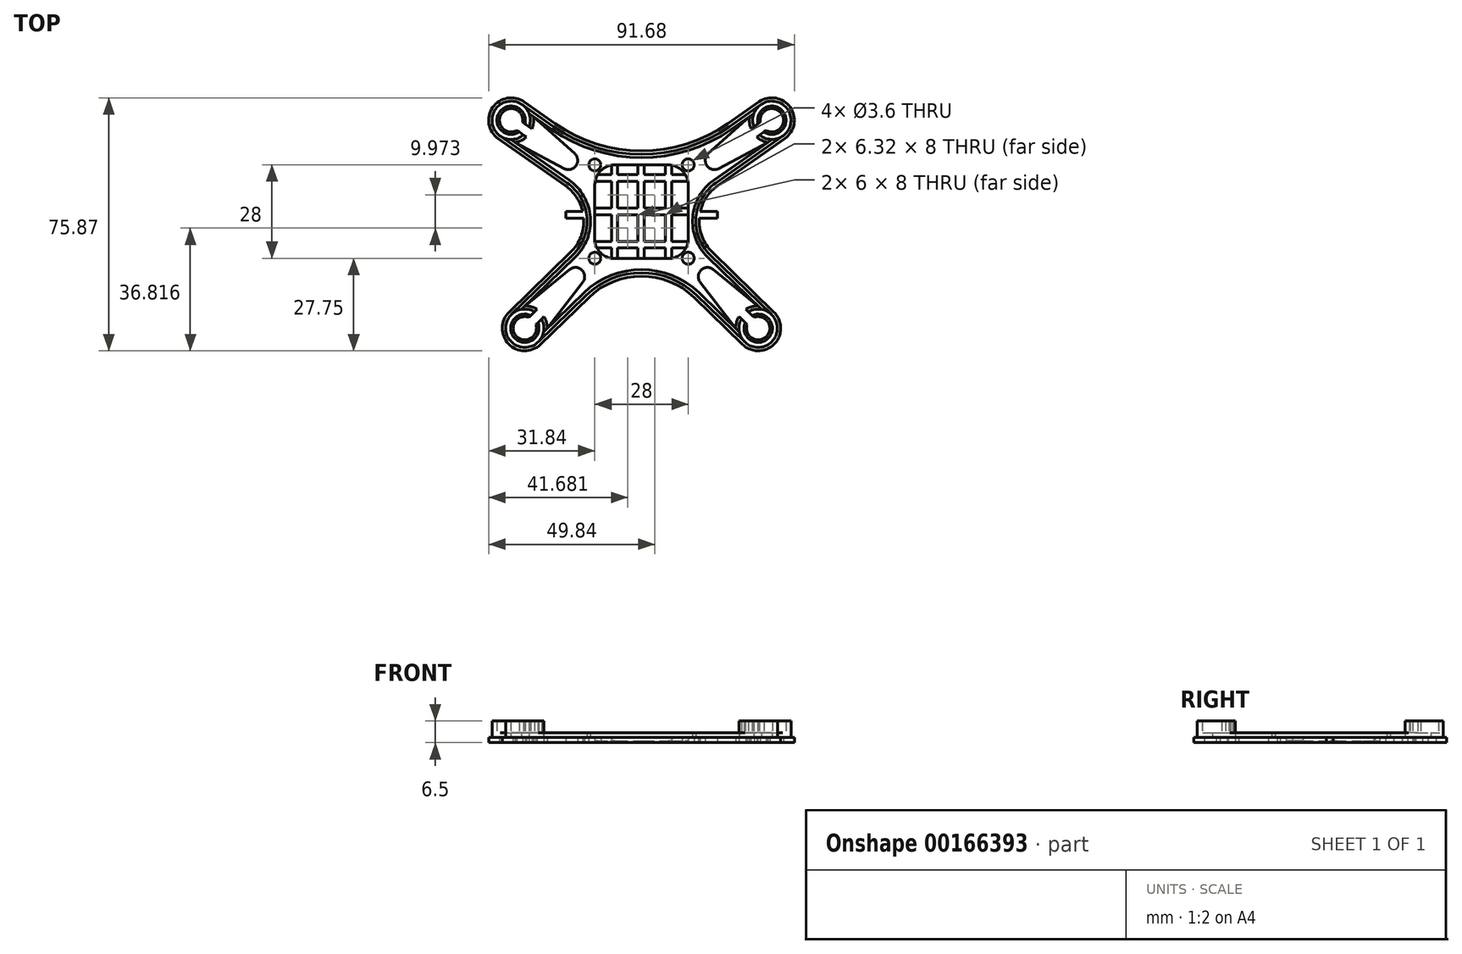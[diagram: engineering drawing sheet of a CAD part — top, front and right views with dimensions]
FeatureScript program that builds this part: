
annotation { "Feature Type Name" : "Feature", "Feature Type Description" : "" }
export const myFeature = defineFeature(function(context is Context, id is Id, definition is map)
    precondition{}
    {
        {
            var Q0;
            Q0=qCreatedBy(makeId("Top.planeOp"),FACE);
            var sketch = newSketch(context, id + "F0", { "sketchPlane" : qUnion([Q0])});
            skArc(sketch, "E0", {"start": v(31.69, -33.87) * mm, "mid": v(37.5, -37.44) * mm, "end": v(33.78, -31.72) * mm});
            skArc(sketch, "E1", {"start": v(29.24, -31.49) * mm, "mid": v(28.5, -33.2) * mm, "end": v(28.25, -35.06) * mm});
            skCircle(sketch, "E2", {"center": v(14, -14) * mm, "radius": 1.8 * mm});
            skLineSegment(sketch, "E3.0", {"start": v(39.7, -30.16) * mm, "end": v(21.24, -12.21) * mm});
            skLineSegment(sketch, "E4.0", {"start": v(30.3, -39.84) * mm, "end": v(15.88, -25.83) * mm});
            skArc(sketch, "E5.MirrorCS", {"start": v(-15.88, -25.83) * mm, "mid": v(0, -19.38) * mm, "end": v(15.88, -25.83) * mm});
            skPoint(sketch, "E6.orphan", {"position": v(7.32, -17.5) * mm});
            skArc(sketch, "E7", {"start": v(21.52, -17.39) * mm, "mid": v(17.87, -17.55) * mm, "end": v(17.6, -21.2) * mm});
            skLineSegment(sketch, "E8", {"start": v(31.69, -33.87) * mm, "end": v(29.24, -31.49) * mm});
            skLineSegment(sketch, "E9", {"start": v(31.33, -29.34) * mm, "end": v(33.78, -31.72) * mm});
            skArc(sketch, "E10.trimOffspring", {"start": v(34.87, -28.25) * mm, "mid": v(33.02, -28.55) * mm, "end": v(31.33, -29.34) * mm});
            skArc(sketch, "E11.trimOffspring", {"start": v(30.3, -39.84) * mm, "mid": v(39.84, -39.7) * mm, "end": v(39.7, -30.16) * mm});
            skArc(sketch, "E12.filletArc", {"start": v(9, -14) * mm, "mid": v(12.31, -12.31) * mm, "end": v(14, -9) * mm});
            skLineSegment(sketch, "E13", {"start": v(28.25, -35.06) * mm, "end": v(17.6, -21.2) * mm});
            skLineSegment(sketch, "E14", {"start": v(34.87, -28.25) * mm, "end": v(21.52, -17.39) * mm});
            skArc(sketch, "E15", {"start": v(37.36, 24.33) * mm, "mid": v(41.96, 29.38) * mm, "end": v(35.64, 26.79) * mm});
            skArc(sketch, "E16", {"start": v(34.56, 22.37) * mm, "mid": v(36.1, 21.32) * mm, "end": v(37.89, 20.73) * mm});
            skLineSegment(sketch, "E17", {"start": v(14, -9) * mm, "end": v(14, 8) * mm});
            skCircle(sketch, "E18", {"center": v(14, 14) * mm, "radius": 1.8 * mm});
            skLineSegment(sketch, "E19", {"start": v(8, 14) * mm, "end": v(0, 14) * mm});
            skArc(sketch, "E20.filletArc", {"start": v(14, 8) * mm, "mid": v(12.24, 12.24) * mm, "end": v(8, 14) * mm});
            skArc(sketch, "E21", {"start": v(20.05, 17.37) * mm, "mid": v(19.64, 13.75) * mm, "end": v(23.18, 12.9) * mm});
            skLineSegment(sketch, "E22.0", {"start": v(22.85, 7.76) * mm, "end": v(42.96, 21.84) * mm});
            skLineSegment(sketch, "E23.0", {"start": v(25.81, 26.31) * mm, "end": v(35.22, 32.9) * mm});
            skLineSegment(sketch, "E24", {"start": v(37.89, 20.73) * mm, "end": v(23.18, 12.9) * mm});
            skLineSegment(sketch, "E25", {"start": v(32.44, 28.51) * mm, "end": v(20.05, 17.37) * mm});
            skLineSegment(sketch, "E26.trimOffspring", {"start": v(34.56, 22.37) * mm, "end": v(37.36, 24.33) * mm});
            skLineSegment(sketch, "E27.trimOffspring", {"start": v(32.84, 24.83) * mm, "end": v(35.64, 26.79) * mm});
            skArc(sketch, "E28.trimOffspring", {"start": v(32.44, 28.51) * mm, "mid": v(32.38, 26.64) * mm, "end": v(32.84, 24.83) * mm});
            skArc(sketch, "E29.trimOffspring", {"start": v(42.96, 21.84) * mm, "mid": v(44.62, 31.24) * mm, "end": v(35.22, 32.9) * mm});
            skArc(sketch, "E30.filletArc", {"start": v(22.85, 7.76) * mm, "mid": v(17.35, -1.85) * mm, "end": v(21.24, -12.21) * mm});
            skArc(sketch, "E31.MirrorCS", {"start": v(-32.44, 28.51) * mm, "mid": v(-32.38, 26.64) * mm, "end": v(-32.84, 24.83) * mm});
            skLineSegment(sketch, "E32.MirrorCS", {"start": v(-32.84, 24.83) * mm, "end": v(-35.64, 26.79) * mm});
            skLineSegment(sketch, "E33.MirrorCS", {"start": v(-34.56, 22.37) * mm, "end": v(-37.36, 24.33) * mm});
            skLineSegment(sketch, "E34.MirrorCS", {"start": v(-31.69, -33.87) * mm, "end": v(-29.24, -31.49) * mm});
            skArc(sketch, "E35.MirrorCS", {"start": v(-34.87, -28.25) * mm, "mid": v(-33.02, -28.55) * mm, "end": v(-31.33, -29.34) * mm});
            skArc(sketch, "E36.MirrorCS", {"start": v(-29.24, -31.49) * mm, "mid": v(-28.5, -33.2) * mm, "end": v(-28.25, -35.06) * mm});
            skArc(sketch, "E37.MirrorCS", {"start": v(-34.56, 22.37) * mm, "mid": v(-36.1, 21.32) * mm, "end": v(-37.89, 20.73) * mm});
            skLineSegment(sketch, "E38.MirrorCS", {"start": v(-31.33, -29.34) * mm, "end": v(-33.78, -31.72) * mm});
            skCircle(sketch, "E39.MirrorC", {"center": v(-14, -14) * mm, "radius": 1.8 * mm});
            skArc(sketch, "E40.MirrorCS", {"start": v(-9, -14) * mm, "mid": v(-12.31, -12.31) * mm, "end": v(-14, -9) * mm});
            skLineSegment(sketch, "E41.MirrorCS", {"start": v(-25.81, 26.31) * mm, "end": v(-35.22, 32.9) * mm});
            skArc(sketch, "E42.MirrorCS", {"start": v(-31.69, -33.87) * mm, "mid": v(-37.5, -37.44) * mm, "end": v(-33.78, -31.72) * mm});
            skLineSegment(sketch, "E43.MirrorCS", {"start": v(-22.85, 7.76) * mm, "end": v(-42.96, 21.84) * mm});
            skLineSegment(sketch, "E44.MirrorCS", {"start": v(-37.89, 20.73) * mm, "end": v(-23.18, 12.9) * mm});
            skPoint(sketch, "E45.MirrorP", {"position": v(-7.32, -17.5) * mm});
            skLineSegment(sketch, "E46.MirrorCS", {"start": v(-14, -9) * mm, "end": v(-14, 8) * mm});
            skCircle(sketch, "E47.MirrorC", {"center": v(-14, 14) * mm, "radius": 1.8 * mm});
            skLineSegment(sketch, "E48.MirrorCS", {"start": v(-32.44, 28.51) * mm, "end": v(-20.05, 17.37) * mm});
            skArc(sketch, "E49.MirrorCS", {"start": v(-21.52, -17.39) * mm, "mid": v(-17.87, -17.55) * mm, "end": v(-17.6, -21.2) * mm});
            skArc(sketch, "E50.MirrorCS", {"start": v(-14, 8) * mm, "mid": v(-12.24, 12.24) * mm, "end": v(-8, 14) * mm});
            skLineSegment(sketch, "E51.MirrorCS", {"start": v(-8, 14) * mm, "end": v(0, 14) * mm});
            skArc(sketch, "E52.MirrorCS", {"start": v(-37.36, 24.33) * mm, "mid": v(-41.96, 29.38) * mm, "end": v(-35.64, 26.79) * mm});
            skArc(sketch, "E53.MirrorCS", {"start": v(-22.85, 7.76) * mm, "mid": v(-17.35, -1.85) * mm, "end": v(-21.24, -12.21) * mm});
            skArc(sketch, "E54.MirrorCS", {"start": v(-20.05, 17.37) * mm, "mid": v(-19.64, 13.75) * mm, "end": v(-23.18, 12.9) * mm});
            skLineSegment(sketch, "E55.MirrorCS", {"start": v(-28.25, -35.06) * mm, "end": v(-17.6, -21.2) * mm});
            skArc(sketch, "E56.MirrorCS", {"start": v(-42.96, 21.84) * mm, "mid": v(-44.62, 31.24) * mm, "end": v(-35.22, 32.9) * mm});
            skLineSegment(sketch, "E57.MirrorCS", {"start": v(-30.3, -39.84) * mm, "end": v(-15.88, -25.83) * mm});
            skLineSegment(sketch, "E58.MirrorCS", {"start": v(-39.7, -30.16) * mm, "end": v(-21.24, -12.21) * mm});
            skLineSegment(sketch, "E59.MirrorCS", {"start": v(-34.87, -28.25) * mm, "end": v(-21.52, -17.39) * mm});
            skArc(sketch, "E60.MirrorCS", {"start": v(-30.3, -39.84) * mm, "mid": v(-39.84, -39.7) * mm, "end": v(-39.7, -30.16) * mm});
            skPoint(sketch, "E61.orphan", {"position": v(-8.23, 14) * mm});
            skPoint(sketch, "E62.orphan", {"position": v(8.23, 14) * mm});
            skArc(sketch, "E63.filletArc", {"start": v(-25.81, 26.31) * mm, "mid": v(0, 18.18) * mm, "end": v(25.81, 26.31) * mm});
            skLineSegment(sketch, "E64.trimOffspring", {"start": v(9, -14) * mm, "end": v(0, -14) * mm});
            skLineSegment(sketch, "E65.trimOffspring", {"start": v(-9, -14) * mm, "end": v(0, -14) * mm});
            skSolve(sketch);
        }
        {
            var Q0;
            Q0=qSketchRegion(id+"F0",true);
            extrude(context, id + "F1", {"entities" : qUnion([Q0]), "depth" : 1.5 * mm});
        }
        {
            var Q0;
            Q0=makeQuery(id+"F1.opExtrude","CAP_FACE",FACE,{"disambiguationData":[OSD([sQuery(id+"F0.wireOp",EDGE,"E0"),sQuery(id+"F0.wireOp",EDGE,"E1"),sQuery(id+"F0.wireOp",EDGE,"a01uJ8fQ-2ShT-JJJs-khPB-feFI2KhJfNbK"),sQuery(id+"F0.wireOp",EDGE,"Ob7BAK0L-Im8b-nV2W-ZPOP-jmZc5u1GQHVQ"),sQuery(id+"F0.wireOp",EDGE,"Yhxhbh3N-Pwvf-CZAK-NTRz-WfjfcWOoB3H8"),sQuery(id+"F0.wireOp",EDGE,"E2"),sQuery(id+"F0.wireOp",EDGE,"E3.0"),sQuery(id+"F0.wireOp",EDGE,"E4.0"),sQuery(id+"F0.wireOp",EDGE,"921c4a34-4074-4e6a-8ea0-2c27b11e1a93.0"),sQuery(id+"F0.wireOp",EDGE,"8042876e-c550-468f-ba5b-50dd2e758e40.0"),sQuery(id+"F0.wireOp",EDGE,"gIcWUmLJ-M7y5-8bh4-X5T4-8Z3JD80z4fvN"),sQuery(id+"F0.wireOp",EDGE,"b88f5849-8e9e-4a16-b14d-f28babdcc0c70.MirrorCS"),sQuery(id+"F0.wireOp",EDGE,"b88f5849-8e9e-4a16-b14d-f28babdcc0c71.MirrorCS"),sQuery(id+"F0.wireOp",EDGE,"b88f5849-8e9e-4a16-b14d-f28babdcc0c74.MirrorCS"),sQuery(id+"F0.wireOp",EDGE,"b88f5849-8e9e-4a16-b14d-f28babdcc0c75.MirrorCS"),sQuery(id+"F0.wireOp",EDGE,"b8554301-71cc-457b-a27f-fdabd42372d80.MirrorCS"),sQuery(id+"F0.wireOp",EDGE,"8d917b84-10ed-46aa-9923-405c7a226399.filletArc"),sQuery(id+"F0.wireOp",EDGE,"E5.MirrorCS"),sQuery(id+"F0.wireOp",EDGE,"a4643b09-8a2d-470e-a5d3-b5b7147de01a.trimOffspring"),sQuery(id+"F0.wireOp",EDGE,"e1d1502e-aa15-4543-9f89-ce20ea1ce206.trimOffspring"),sQuery(id+"F0.wireOp",EDGE,"E7"),sQuery(id+"F0.wireOp",EDGE,"432c7407-925d-4150-9526-7c587b8a6b590.MirrorCS"),sQuery(id+"F0.wireOp",EDGE,"432c7407-925d-4150-9526-7c587b8a6b591.MirrorCS"),sQuery(id+"F0.wireOp",EDGE,"432c7407-925d-4150-9526-7c587b8a6b592.MirrorCS"),sQuery(id+"F0.wireOp",EDGE,"84ef0a4b-eb97-41a7-a49f-92f9b87771770.MirrorCS"),sQuery(id+"F0.wireOp",EDGE,"84ef0a4b-eb97-41a7-a49f-92f9b87771771.MirrorCS"),sQuery(id+"F0.wireOp",EDGE,"84ef0a4b-eb97-41a7-a49f-92f9b87771772.MirrorCS"),sQuery(id+"F0.wireOp",EDGE,"84ef0a4b-eb97-41a7-a49f-92f9b87771773.MirrorCS"),sQuery(id+"F0.wireOp",EDGE,"84ef0a4b-eb97-41a7-a49f-92f9b87771774.MirrorCS"),sQuery(id+"F0.wireOp",EDGE,"84ef0a4b-eb97-41a7-a49f-92f9b87771775.MirrorCS"),sQuery(id+"F0.wireOp",EDGE,"feb3afbb-cc8c-4bbc-aa67-0586ad6dce8c.0"),sQuery(id+"F0.wireOp",EDGE,"a1452b85-d45b-435e-881a-8c6a6ef33bc9.0"),sQuery(id+"F0.wireOp",EDGE,"64c3a18d-b4ba-416d-8e09-7861b4cc0028.0"),sQuery(id+"F0.wireOp",EDGE,"76b5986a-2c51-4484-8229-e95649198d5d.0"),sQuery(id+"F0.wireOp",EDGE,"E8"),sQuery(id+"F0.wireOp",EDGE,"E9"),sQuery(id+"F0.wireOp",EDGE,"E10.trimOffspring"),sQuery(id+"F0.wireOp",EDGE,"E11.trimOffspring"),sQuery(id+"F0.wireOp",EDGE,"e6a221e6-ec1e-47e5-89df-8c310038d3240.MirrorCS"),sQuery(id+"F0.wireOp",EDGE,"e6a221e6-ec1e-47e5-89df-8c310038d3241.MirrorCS"),sQuery(id+"F0.wireOp",EDGE,"e6a221e6-ec1e-47e5-89df-8c310038d3242.MirrorCS"),sQuery(id+"F0.wireOp",EDGE,"e6a221e6-ec1e-47e5-89df-8c310038d3244.MirrorCS"),sQuery(id+"F0.wireOp",EDGE,"e6a221e6-ec1e-47e5-89df-8c310038d3245.MirrorCS"),sQuery(id+"F0.wireOp",EDGE,"e6a221e6-ec1e-47e5-89df-8c310038d3246.MirrorCS"),sQuery(id+"F0.wireOp",EDGE,"1c5d13f6-029d-4adf-95b2-7eb6a2bd37fe0.MirrorCS"),sQuery(id+"F0.wireOp",EDGE,"1c5d13f6-029d-4adf-95b2-7eb6a2bd37fe1.MirrorCS"),sQuery(id+"F0.wireOp",EDGE,"1c5d13f6-029d-4adf-95b2-7eb6a2bd37fe2.MirrorCS"),sQuery(id+"F0.wireOp",EDGE,"1c5d13f6-029d-4adf-95b2-7eb6a2bd37fe3.MirrorCS"),sQuery(id+"F0.wireOp",EDGE,"1c5d13f6-029d-4adf-95b2-7eb6a2bd37fe5.MirrorCS"),sQuery(id+"F0.wireOp",EDGE,"1c5d13f6-029d-4adf-95b2-7eb6a2bd37fe6.MirrorCS"),sQuery(id+"F0.wireOp",EDGE,"1c5d13f6-029d-4adf-95b2-7eb6a2bd37fe7.MirrorCS"),sQuery(id+"F0.wireOp",EDGE,"1c5d13f6-029d-4adf-95b2-7eb6a2bd37fe8.MirrorCS"),sQuery(id+"F0.wireOp",EDGE,"1c5d13f6-029d-4adf-95b2-7eb6a2bd37fe9.MirrorCS"),sQuery(id+"F0.wireOp",EDGE,"1c5d13f6-029d-4adf-95b2-7eb6a2bd37fe10.MirrorCS"),sQuery(id+"F0.wireOp",EDGE,"1c5d13f6-029d-4adf-95b2-7eb6a2bd37fe12.MirrorCS"),sQuery(id+"F0.wireOp",EDGE,"1c5d13f6-029d-4adf-95b2-7eb6a2bd37fe13.MirrorCS")])],"isStart":false});
            var sketch = newSketch(context, id + "F2", { "sketchPlane" : qUnion([Q0])});
            skLineSegment(sketch, "E66.0", {"start": v(32.07, -30.06) * mm, "end": v(33.2, -31.15) * mm});
            skLineSegment(sketch, "E66.1", {"start": v(31.1, -33.3) * mm, "end": v(29.97, -32.2) * mm});
            skArc(sketch, "E67", {"start": v(31.1, -33.3) * mm, "mid": v(38.05, -37.96) * mm, "end": v(33.2, -31.15) * mm});
            skArc(sketch, "E68", {"start": v(29.97, -32.2) * mm, "mid": v(39.12, -39) * mm, "end": v(32.07, -30.06) * mm});
            skLineSegment(sketch, "E69.MirrorCS", {"start": v(-32.07, -30.06) * mm, "end": v(-33.2, -31.15) * mm});
            skLineSegment(sketch, "E70.MirrorCS", {"start": v(-31.1, -33.3) * mm, "end": v(-29.97, -32.2) * mm});
            skArc(sketch, "E71.MirrorCS", {"start": v(-31.1, -33.3) * mm, "mid": v(-38.05, -37.96) * mm, "end": v(-33.2, -31.15) * mm});
            skArc(sketch, "E72.MirrorCS", {"start": v(-29.97, -32.2) * mm, "mid": v(-39.12, -39) * mm, "end": v(-32.07, -30.06) * mm});
            skArc(sketch, "E73.0", {"start": v(37.36, 24.33) * mm, "mid": v(41.96, 29.38) * mm, "end": v(35.64, 26.79) * mm});
            skArc(sketch, "E74", {"start": v(36.7, 23.86) * mm, "mid": v(42.57, 29.8) * mm, "end": v(34.97, 26.32) * mm});
            skArc(sketch, "E75", {"start": v(35.4, 22.96) * mm, "mid": v(43.8, 30.67) * mm, "end": v(33.68, 25.42) * mm});
            skLineSegment(sketch, "E76.0", {"start": v(35.4, 22.96) * mm, "end": v(36.7, 23.86) * mm});
            skLineSegment(sketch, "E76.2", {"start": v(33.68, 25.42) * mm, "end": v(34.97, 26.32) * mm});
            skPoint(sketch, "E77.orphan", {"position": v(34.56, 22.37) * mm});
            skPoint(sketch, "E78.orphan", {"position": v(32.84, 24.83) * mm});
            skLineSegment(sketch, "E79.MirrorCS", {"start": v(-35.4, 22.96) * mm, "end": v(-36.7, 23.86) * mm});
            skLineSegment(sketch, "E80.MirrorCS", {"start": v(-33.68, 25.42) * mm, "end": v(-34.97, 26.32) * mm});
            skArc(sketch, "E81.MirrorCS", {"start": v(-36.7, 23.86) * mm, "mid": v(-42.57, 29.8) * mm, "end": v(-34.97, 26.32) * mm});
            skArc(sketch, "E82.MirrorCS", {"start": v(-37.36, 24.33) * mm, "mid": v(-41.96, 29.38) * mm, "end": v(-35.64, 26.79) * mm});
            skPoint(sketch, "E83.MirrorP", {"position": v(-32.84, 24.83) * mm});
            skArc(sketch, "E84.MirrorCS", {"start": v(-35.4, 22.96) * mm, "mid": v(-43.8, 30.67) * mm, "end": v(-33.68, 25.42) * mm});
            skPoint(sketch, "E85.MirrorP", {"position": v(-34.56, 22.37) * mm});
            skSolve(sketch);
        }
        {
            var Q0;
            Q0=qSketchRegion(id+"F2",true);
            extrude(context, id + "F3", {"entities" : qUnion([Q0]), "operationType" : NewBodyOperationType.ADD, "depth" : 5 * mm});
        }
        {
            var Q0;
            Q0=qCreatedBy(makeId("Top.planeOp"),FACE);
            var sketch = newSketch(context, id + "F4", { "sketchPlane" : qUnion([Q0])});
            skLineSegment(sketch, "E86.0", {"start": v(0.84, -8.93) * mm, "end": v(0.84, -0.93) * mm});
            skLineSegment(sketch, "E87.0", {"start": v(-1.16, -8.93) * mm, "end": v(-1.16, -0.93) * mm});
            skLineSegment(sketch, "E88.1.0.0", {"start": v(7.16, -8.93) * mm, "end": v(7.16, -0.93) * mm});
            skLineSegment(sketch, "E88.1.0.1", {"start": v(9, -14) * mm, "end": v(9, -10.93) * mm});
            skLineSegment(sketch, "E89.MirrorCS", {"start": v(-7.16, -8.93) * mm, "end": v(-7.16, -0.93) * mm});
            skLineSegment(sketch, "E90.MirrorCS", {"start": v(-9, -8.93) * mm, "end": v(-9, -0.93) * mm});
            skLineSegment(sketch, "E91.0", {"start": v(-14, 1.04) * mm, "end": v(-9, 1.04) * mm});
            skLineSegment(sketch, "E92.0", {"start": v(-14, -0.93) * mm, "end": v(-9, -0.93) * mm});
            skLineSegment(sketch, "E93.0", {"start": v(-14, 9.04) * mm, "end": v(-9, 9.04) * mm});
            skLineSegment(sketch, "E94.0", {"start": v(-13.57, 11.04) * mm, "end": v(-9, 11.04) * mm});
            skLineSegment(sketch, "E95.0", {"start": v(-14, -8.93) * mm, "end": v(-9, -8.93) * mm});
            skLineSegment(sketch, "E96.0", {"start": v(-13.61, -10.93) * mm, "end": v(-9, -10.93) * mm});
            skPoint(sketch, "E97.5", {"position": v(9, -14) * mm});
            skPoint(sketch, "E98.orphan", {"position": v(-9, 14.56) * mm});
            skPoint(sketch, "E99.orphan", {"position": v(-7.16, 14.62) * mm});
            skPoint(sketch, "E100.orphan", {"position": v(0.84, 14.62) * mm});
            skPoint(sketch, "E101.orphan", {"position": v(-1.16, 14.62) * mm});
            skPoint(sketch, "E102.orphan", {"position": v(7.16, 14.62) * mm});
            skPoint(sketch, "E103.orphan", {"position": v(9, 14.56) * mm});
            skPoint(sketch, "E104.orphan", {"position": v(9, -14.52) * mm});
            skPoint(sketch, "E105.orphan", {"position": v(0.84, -14.46) * mm});
            skPoint(sketch, "E106.orphan", {"position": v(-7.16, -14.46) * mm});
            skPoint(sketch, "E107.orphan", {"position": v(-9, -14.52) * mm});
            skLineSegment(sketch, "E108.trimOffspring", {"start": v(-7.16, 11.04) * mm, "end": v(-1.16, 11.04) * mm});
            skLineSegment(sketch, "E109.trimOffspring", {"start": v(-7.16, 11.04) * mm, "end": v(-7.16, 14) * mm});
            skLineSegment(sketch, "E110.trimOffspring", {"start": v(-7.16, 9.04) * mm, "end": v(-1.16, 9.04) * mm});
            skLineSegment(sketch, "E111.trimOffspring", {"start": v(-9, 11.04) * mm, "end": v(-9, 14) * mm});
            skLineSegment(sketch, "E112.trimOffspring", {"start": v(-1.16, 11.04) * mm, "end": v(-1.16, 14) * mm});
            skLineSegment(sketch, "E113.trimOffspring", {"start": v(0.84, 11.04) * mm, "end": v(0.84, 14) * mm});
            skLineSegment(sketch, "E114.trimOffspring", {"start": v(0.84, 9.04) * mm, "end": v(7.16, 9.04) * mm});
            skLineSegment(sketch, "E115.trimOffspring", {"start": v(0.84, 11.04) * mm, "end": v(7.16, 11.04) * mm});
            skLineSegment(sketch, "E116.trimOffspring", {"start": v(9, 11.04) * mm, "end": v(13.64, 11.04) * mm});
            skLineSegment(sketch, "E117.trimOffspring", {"start": v(9, 9.04) * mm, "end": v(14, 9.04) * mm});
            skLineSegment(sketch, "E118.trimOffspring", {"start": v(9, 11.04) * mm, "end": v(9, 14) * mm});
            skLineSegment(sketch, "E119.trimOffspring", {"start": v(7.16, 11.04) * mm, "end": v(7.16, 14) * mm});
            skLineSegment(sketch, "E120.trimOffspring", {"start": v(9, -0.93) * mm, "end": v(14, -0.93) * mm});
            skLineSegment(sketch, "E121.trimOffspring", {"start": v(0.84, 1.04) * mm, "end": v(7.16, 1.04) * mm});
            skLineSegment(sketch, "E122.trimOffspring", {"start": v(0.84, -0.93) * mm, "end": v(7.16, -0.93) * mm});
            skLineSegment(sketch, "E123.trimOffspring", {"start": v(9, 1.04) * mm, "end": v(14, 1.04) * mm});
            skLineSegment(sketch, "E124.trimOffspring", {"start": v(-7.16, 1.04) * mm, "end": v(-1.16, 1.04) * mm});
            skLineSegment(sketch, "E125.trimOffspring", {"start": v(-7.16, -0.93) * mm, "end": v(-1.16, -0.93) * mm});
            skLineSegment(sketch, "E126.trimOffspring", {"start": v(-7.16, -8.93) * mm, "end": v(-1.16, -8.93) * mm});
            skLineSegment(sketch, "E127.trimOffspring", {"start": v(9, -8.93) * mm, "end": v(9, -0.93) * mm});
            skLineSegment(sketch, "E128.trimOffspring", {"start": v(0.84, -8.93) * mm, "end": v(7.16, -8.93) * mm});
            skLineSegment(sketch, "E129", {"start": v(-7.16, -10.93) * mm, "end": v(-7.16, -14) * mm});
            skLineSegment(sketch, "E130.trimOffspring", {"start": v(-7.16, -10.93) * mm, "end": v(-1.16, -10.93) * mm});
            skLineSegment(sketch, "E131.trimOffspring", {"start": v(-9, -10.93) * mm, "end": v(-9, -14) * mm});
            skLineSegment(sketch, "E132", {"start": v(-1.16, -10.93) * mm, "end": v(-1.16, -14) * mm});
            skLineSegment(sketch, "E133", {"start": v(0.84, -10.93) * mm, "end": v(0.84, -14) * mm});
            skLineSegment(sketch, "E134", {"start": v(7.16, -10.93) * mm, "end": v(7.16, -14) * mm});
            skLineSegment(sketch, "E135.trimOffspring", {"start": v(0.84, -10.93) * mm, "end": v(7.16, -10.93) * mm});
            skLineSegment(sketch, "E136.trimOffspring", {"start": v(9, -10.93) * mm, "end": v(13.61, -10.93) * mm});
            skLineSegment(sketch, "E137.trimOffspring", {"start": v(7.16, 1.04) * mm, "end": v(7.16, 9.04) * mm});
            skLineSegment(sketch, "E138.trimOffspring", {"start": v(9, 1.04) * mm, "end": v(9, 9.04) * mm});
            skLineSegment(sketch, "E139.trimOffspring", {"start": v(-7.16, 1.04) * mm, "end": v(-7.16, 9.04) * mm});
            skLineSegment(sketch, "E140.trimOffspring", {"start": v(-9, 1.04) * mm, "end": v(-9, 9.04) * mm});
            skLineSegment(sketch, "E141.trimOffspring", {"start": v(-1.16, 1.04) * mm, "end": v(-1.16, 9.04) * mm});
            skLineSegment(sketch, "E142.trimOffspring", {"start": v(0.84, 1.04) * mm, "end": v(0.84, 9.04) * mm});
            skPoint(sketch, "E143.orphan", {"position": v(7.16, -14.46) * mm});
            skLineSegment(sketch, "E144.0", {"start": v(-9, -14) * mm, "end": v(9, -14) * mm});
            skLineSegment(sketch, "E144.1", {"start": v(9, -14) * mm, "end": v(9, -14) * mm});
            skLineSegment(sketch, "E144.2", {"start": v(14, 9) * mm, "end": v(14, -9) * mm});
            skArc(sketch, "E144.3", {"start": v(9, 14) * mm, "mid": v(12.54, 12.54) * mm, "end": v(14, 9) * mm});
            skLineSegment(sketch, "E144.4", {"start": v(-9, 14) * mm, "end": v(9, 14) * mm});
            skArc(sketch, "E144.5", {"start": v(-9, 14) * mm, "mid": v(-12.54, 12.54) * mm, "end": v(-14, 9) * mm});
            skLineSegment(sketch, "E144.6", {"start": v(-14, 9) * mm, "end": v(-14, -9) * mm});
            skArc(sketch, "E144.7", {"start": v(-9, -14) * mm, "mid": v(-12.54, -12.54) * mm, "end": v(-14, -9) * mm});
            skPoint(sketch, "E144.8", {"position": v(-12.54, -12.54) * mm});
            skLineSegment(sketch, "E145", {"start": v(9, -8.93) * mm, "end": v(14, -8.93) * mm});
            skLineSegment(sketch, "E146.trimOffspring", {"start": v(-9, 14.56) * mm, "end": v(-9, 14.63) * mm});
            skArc(sketch, "E147.2", {"start": v(9, -14) * mm, "mid": v(12.31, -12.31) * mm, "end": v(14, -9) * mm});
            skSolve(sketch);
        }
        {
            var Q0;
            Q0=makeQuery(id+"F4.imprint","IMPRINT",FACE,{"disambiguationData":[TD([[makeQuery(id+"F4.imprint","IMPRINT",EDGE,{"derivedFrom":sQuery(id+"F4.wireOp",EDGE,"E86.0")}),1.0]])]});
            extrude(context, id + "F5", {"entities" : qUnion([Q0]), "operationType" : NewBodyOperationType.ADD, "depth" : .5 * mm});
        }
        {
            var Q0;
            {var subQ0=sQuery(id+"F0.wireOp",EDGE,"6d079c65-f35f-44f5-b430-592cdccd792f22.MirrorCS");var subQ1=sQuery(id+"F0.wireOp",EDGE,"6d079c65-f35f-44f5-b430-592cdccd792f17.MirrorCS");var subQ2=sQuery(id+"F0.wireOp",EDGE,"6d079c65-f35f-44f5-b430-592cdccd792f13.MirrorCS");var subQ3=sQuery(id+"F0.wireOp",EDGE,"6d079c65-f35f-44f5-b430-592cdccd792f21.MirrorCS");var subQ4=sQuery(id+"F0.wireOp",EDGE,"6d079c65-f35f-44f5-b430-592cdccd792f11.MirrorCS");var subQ5=sQuery(id+"F0.wireOp",EDGE,"6d079c65-f35f-44f5-b430-592cdccd792f12.MirrorCS");var subQ6=sQuery(id+"F0.wireOp",EDGE,"6d079c65-f35f-44f5-b430-592cdccd792f10.MirrorCS");var subQ7=sQuery(id+"F0.wireOp",EDGE,"6d079c65-f35f-44f5-b430-592cdccd792f18.MirrorCS");var subQ8=sQuery(id+"F0.wireOp",EDGE,"6d079c65-f35f-44f5-b430-592cdccd792f7.MirrorCS");var subQ9=sQuery(id+"F0.wireOp",EDGE,"6d079c65-f35f-44f5-b430-592cdccd792f5.MirrorC");var subQ10=sQuery(id+"F0.wireOp",EDGE,"6d079c65-f35f-44f5-b430-592cdccd792f3.MirrorCS");var subQ11=sQuery(id+"F0.wireOp",EDGE,"6d079c65-f35f-44f5-b430-592cdccd792f1.MirrorCS");var subQ12=sQuery(id+"F0.wireOp",EDGE,"902b4b71-a90e-46d3-8408-61ad1edd732f11.MirrorCS");var subQ13=sQuery(id+"F0.wireOp",EDGE,"902b4b71-a90e-46d3-8408-61ad1edd732f14.MirrorCS");var subQ14=sQuery(id+"F0.wireOp",EDGE,"6d079c65-f35f-44f5-b430-592cdccd792f20.MirrorCS");var subQ15=sQuery(id+"F0.wireOp",EDGE,"6d079c65-f35f-44f5-b430-592cdccd792f8.MirrorCS");var subQ16=sQuery(id+"F0.wireOp",EDGE,"6d079c65-f35f-44f5-b430-592cdccd792f6.MirrorCS");var subQ17=sQuery(id+"F0.wireOp",EDGE,"902b4b71-a90e-46d3-8408-61ad1edd732f13.MirrorCS");var subQ18=sQuery(id+"F0.wireOp",EDGE,"902b4b71-a90e-46d3-8408-61ad1edd732f12.MirrorC");var subQ19=sQuery(id+"F0.wireOp",EDGE,"6d079c65-f35f-44f5-b430-592cdccd792f4.MirrorCS");var subQ20=sQuery(id+"F0.wireOp",EDGE,"6d079c65-f35f-44f5-b430-592cdccd792f2.MirrorC");var subQ21=sQuery(id+"F0.wireOp",EDGE,"902b4b71-a90e-46d3-8408-61ad1edd732f10.MirrorCS");var subQ22=sQuery(id+"F0.wireOp",EDGE,"E9");var subQ23=sQuery(id+"F0.wireOp",EDGE,"E7");var subQ24=sQuery(id+"F0.wireOp",EDGE,"6d079c65-f35f-44f5-b430-592cdccd792f36.MirrorCS");var subQ25=sQuery(id+"F0.wireOp",EDGE,"E14");var subQ26=sQuery(id+"F0.wireOp",EDGE,"E5.MirrorCS");var subQ27=sQuery(id+"F0.wireOp",EDGE,"gIcWUmLJ-M7y5-8bh4-X5T4-8Z3JD80z4fvN");var subQ28=sQuery(id+"F0.wireOp",EDGE,"902b4b71-a90e-46d3-8408-61ad1edd732f2.MirrorCS");var subQ29=sQuery(id+"F0.wireOp",EDGE,"E8");var subQ30=sQuery(id+"F0.wireOp",EDGE,"E1");var subQ31=sQuery(id+"F0.wireOp",EDGE,"E2");var subQ32=sQuery(id+"F0.wireOp",EDGE,"6d079c65-f35f-44f5-b430-592cdccd792f16.MirrorCS");var subQ33=sQuery(id+"F0.wireOp",EDGE,"E3.0");var subQ34=sQuery(id+"F0.wireOp",EDGE,"E4.0");var subQ35=sQuery(id+"F0.wireOp",EDGE,"902b4b71-a90e-46d3-8408-61ad1edd732f8.MirrorCS");var subQ36=sQuery(id+"F0.wireOp",EDGE,"E11.trimOffspring");var subQ37=sQuery(id+"F0.wireOp",EDGE,"902b4b71-a90e-46d3-8408-61ad1edd732f1.MirrorCS");var subQ38=sQuery(id+"F0.wireOp",EDGE,"6d079c65-f35f-44f5-b430-592cdccd792f35.MirrorCS");var subQ39=sQuery(id+"F0.wireOp",EDGE,"902b4b71-a90e-46d3-8408-61ad1edd732f3.MirrorCS");var subQ40=sQuery(id+"F0.wireOp",EDGE,"E10.trimOffspring");var subQ41=sQuery(id+"F0.wireOp",EDGE,"902b4b71-a90e-46d3-8408-61ad1edd732f4.MirrorCS");var subQ42=sQuery(id+"F0.wireOp",EDGE,"902b4b71-a90e-46d3-8408-61ad1edd732f16.MirrorCS");var subQ43=sQuery(id+"F0.wireOp",EDGE,"902b4b71-a90e-46d3-8408-61ad1edd732f7.MirrorCS");var subQ44=sQuery(id+"F0.wireOp",EDGE,"902b4b71-a90e-46d3-8408-61ad1edd732f5.MirrorCS");var subQ45=sQuery(id+"F0.wireOp",EDGE,"E13");var subQ46=sQuery(id+"F0.wireOp",EDGE,"E12.filletArc");var subQ47=sQuery(id+"F0.wireOp",EDGE,"902b4b71-a90e-46d3-8408-61ad1edd732f6.MirrorCS");var subQ48=sQuery(id+"F0.wireOp",EDGE,"6d079c65-f35f-44f5-b430-592cdccd792f23.MirrorCS");var subQ49=sQuery(id+"F0.wireOp",EDGE,"6d079c65-f35f-44f5-b430-592cdccd792f25.MirrorCS");var subQ50=sQuery(id+"F0.wireOp",EDGE,"6d079c65-f35f-44f5-b430-592cdccd792f26.MirrorCS");var subQ51=sQuery(id+"F0.wireOp",EDGE,"6d079c65-f35f-44f5-b430-592cdccd792f27.MirrorCS");var subQ52=sQuery(id+"F0.wireOp",EDGE,"6d079c65-f35f-44f5-b430-592cdccd792f29.MirrorCS");var subQ53=sQuery(id+"F0.wireOp",EDGE,"6d079c65-f35f-44f5-b430-592cdccd792f31.MirrorCS");var subQ54=sQuery(id+"F0.wireOp",EDGE,"6d079c65-f35f-44f5-b430-592cdccd792f32.MirrorCS");var subQ55=sQuery(id+"F0.wireOp",EDGE,"6d079c65-f35f-44f5-b430-592cdccd792f34.MirrorCS");Q0=makeQuery(id+"F3.boolean.opBoolean","SPLIT",FACE,{"disambiguationData":[TD([makeQuery(id+"F1.opExtrude","SWEPT_FACE",FACE,{"disambiguationData":[OSD([subQ30])]})])],"derivedFrom":makeQuery(id+"F1.opExtrude","CAP_FACE",FACE,{"disambiguationData":[OSD([sQuery(id+"F0.wireOp",EDGE,"E0"),subQ30,subQ31,subQ33,subQ34,subQ27,subQ26,subQ23,subQ29,subQ22,subQ40,subQ36,subQ46,subQ45,subQ25,subQ37,subQ28,subQ39,subQ41,subQ44,subQ47,subQ43,subQ35,sQuery(id+"F0.wireOp",EDGE,"902b4b71-a90e-46d3-8408-61ad1edd732f9.MirrorCS"),subQ21,subQ12,subQ18,subQ17,subQ13,subQ42,subQ11,subQ20,subQ10,subQ19,subQ9,subQ16,subQ8,subQ15,subQ6,subQ4,subQ5,subQ2,subQ32,subQ1,subQ7,subQ14,subQ3,subQ0,subQ48,sQuery(id+"F0.wireOp",EDGE,"6d079c65-f35f-44f5-b430-592cdccd792f24.MirrorCS"),subQ49,subQ50,subQ51,sQuery(id+"F0.wireOp",EDGE,"6d079c65-f35f-44f5-b430-592cdccd792f28.MirrorCS"),subQ52,subQ53,subQ54,subQ55,subQ38,subQ24])],"isStart":false})});}
            var sketch = newSketch(context, id + "F6", { "sketchPlane" : qUnion([Q0])});
            skLineSegment(sketch, "E148.0", {"start": v(-31, -39.12) * mm, "end": v(-16.58, -25.11) * mm});
            skArc(sketch, "E148.1", {"start": v(-16.58, -25.11) * mm, "mid": v(0, -18.38) * mm, "end": v(16.58, -25.11) * mm});
            skLineSegment(sketch, "E148.2", {"start": v(31, -39.12) * mm, "end": v(16.58, -25.11) * mm});
            skLineSegment(sketch, "E149.0", {"start": v(-29.37, -36.15) * mm, "end": v(-17.28, -24.4) * mm});
            skArc(sketch, "E149.1", {"start": v(-17.28, -24.4) * mm, "mid": v(0, -17.38) * mm, "end": v(17.28, -24.4) * mm});
            skLineSegment(sketch, "E149.2", {"start": v(29.37, -36.15) * mm, "end": v(17.28, -24.4) * mm});
            skArc(sketch, "E150.1", {"start": v(-29.37, -36.15) * mm, "mid": v(-29.95, -37.76) * mm, "end": v(-31, -39.12) * mm});
            skArc(sketch, "E150.2", {"start": v(29.37, -36.15) * mm, "mid": v(29.95, -37.76) * mm, "end": v(31, -39.12) * mm});
            skArc(sketch, "E151.trimOffspring", {"start": v(39, -30.88) * mm, "mid": v(37.61, -29.88) * mm, "end": v(35.99, -29.34) * mm});
            skArc(sketch, "E152.trimOffspring", {"start": v(-39, -30.88) * mm, "mid": v(-37.61, -29.88) * mm, "end": v(-35.99, -29.34) * mm});
            skPoint(sketch, "E153.orphan", {"position": v(32.07, -30.06) * mm});
            skPoint(sketch, "E154.orphan", {"position": v(29.97, -32.2) * mm});
            skPoint(sketch, "E155.orphan", {"position": v(-29.97, -32.2) * mm});
            skPoint(sketch, "E156.orphan", {"position": v(-32.07, -30.06) * mm});
            skLineSegment(sketch, "E157.0", {"start": v(39.7, -30.16) * mm, "end": v(21.24, -12.21) * mm});
            skArc(sketch, "E157.1", {"start": v(22.85, 7.76) * mm, "mid": v(17.35, -1.85) * mm, "end": v(21.24, -12.21) * mm});
            skLineSegment(sketch, "E157.2", {"start": v(22.85, 7.76) * mm, "end": v(42.96, 21.84) * mm});
            skArc(sketch, "E157.3", {"start": v(-25.81, 26.31) * mm, "mid": v(0, 18.18) * mm, "end": v(25.81, 26.31) * mm});
            skLineSegment(sketch, "E157.4", {"start": v(25.81, 26.31) * mm, "end": v(35.22, 32.9) * mm});
            skLineSegment(sketch, "E157.5", {"start": v(-25.81, 26.31) * mm, "end": v(-35.22, 32.9) * mm});
            skArc(sketch, "E157.6", {"start": v(-22.85, 7.76) * mm, "mid": v(-17.35, -1.85) * mm, "end": v(-21.24, -12.21) * mm});
            skLineSegment(sketch, "E157.7", {"start": v(-22.85, 7.76) * mm, "end": v(-42.96, 21.84) * mm});
            skLineSegment(sketch, "E157.8", {"start": v(-39.7, -30.16) * mm, "end": v(-21.24, -12.21) * mm});
            skPoint(sketch, "E157.9", {"position": v(-32.9, 14.8) * mm});
            skLineSegment(sketch, "E158.0", {"start": v(-26.38, 25.5) * mm, "end": v(-35.8, 32.08) * mm});
            skArc(sketch, "E158.1", {"start": v(-26.38, 25.5) * mm, "mid": v(0, 17.18) * mm, "end": v(26.38, 25.5) * mm});
            skLineSegment(sketch, "E158.2", {"start": v(26.38, 25.5) * mm, "end": v(35.8, 32.08) * mm});
            skLineSegment(sketch, "E159.0", {"start": v(26.96, 24.67) * mm, "end": v(33.71, 29.4) * mm});
            skArc(sketch, "E159.1", {"start": v(-26.96, 24.67) * mm, "mid": v(0, 16.18) * mm, "end": v(26.96, 24.67) * mm});
            skLineSegment(sketch, "E159.2", {"start": v(-26.96, 24.67) * mm, "end": v(-33.71, 29.4) * mm});
            skLineSegment(sketch, "E160.0", {"start": v(22.28, 8.58) * mm, "end": v(42.39, 22.66) * mm});
            skArc(sketch, "E160.1", {"start": v(22.28, 8.58) * mm, "mid": v(16.35, -1.77) * mm, "end": v(20.55, -12.93) * mm});
            skLineSegment(sketch, "E160.2", {"start": v(39, -30.88) * mm, "end": v(20.55, -12.93) * mm});
            skLineSegment(sketch, "E161.0", {"start": v(21.7, 9.4) * mm, "end": v(39.16, 21.62) * mm});
            skArc(sketch, "E161.1", {"start": v(21.7, 9.4) * mm, "mid": v(15.35, -1.69) * mm, "end": v(19.85, -13.65) * mm});
            skLineSegment(sketch, "E161.2", {"start": v(35.99, -29.34) * mm, "end": v(19.85, -13.65) * mm});
            skLineSegment(sketch, "E162.0", {"start": v(-22.28, 8.58) * mm, "end": v(-42.39, 22.66) * mm});
            skArc(sketch, "E162.1", {"start": v(-22.28, 8.58) * mm, "mid": v(-16.35, -1.77) * mm, "end": v(-20.55, -12.93) * mm});
            skLineSegment(sketch, "E162.2", {"start": v(-39, -30.88) * mm, "end": v(-20.55, -12.93) * mm});
            skLineSegment(sketch, "E163.0", {"start": v(-21.7, 9.4) * mm, "end": v(-39.16, 21.62) * mm});
            skArc(sketch, "E163.1", {"start": v(-21.7, 9.4) * mm, "mid": v(-15.35, -1.69) * mm, "end": v(-19.85, -13.65) * mm});
            skLineSegment(sketch, "E163.2", {"start": v(-35.99, -29.34) * mm, "end": v(-19.85, -13.65) * mm});
            skArc(sketch, "E164.0", {"start": v(39.16, 21.62) * mm, "mid": v(40.85, 21.9) * mm, "end": v(42.39, 22.66) * mm});
            skArc(sketch, "E164.1", {"start": v(-29.97, -32.2) * mm, "mid": v(-29.31, -35.84) * mm, "end": v(-31, -39.12) * mm});
            skArc(sketch, "E164.2", {"start": v(-35.4, 22.96) * mm, "mid": v(-38.85, 21.63) * mm, "end": v(-42.39, 22.66) * mm});
            skArc(sketch, "E165.trimOffspring", {"start": v(35.8, 32.08) * mm, "mid": v(33.6, 29.1) * mm, "end": v(33.68, 25.42) * mm});
            skPoint(sketch, "E166.orphan", {"position": v(35.4, 22.96) * mm});
            skArc(sketch, "E167.trimOffspring", {"start": v(-35.8, 32.08) * mm, "mid": v(-33.6, 29.1) * mm, "end": v(-33.68, 25.42) * mm});
            skSolve(sketch);
        }
        {
            var Q0;
            Q0=qSketchRegion(id+"F6",true);
            extrude(context, id + "F7", {"entities" : qUnion([Q0]), "operationType" : NewBodyOperationType.ADD, "depth" : 1.5 * mm});
        }
        {
            var Q0;
            Q0=makeQuery(id+"F4.imprint","IMPRINT",FACE,{"disambiguationData":[TD([[makeQuery(id+"F4.imprint","IMPRINT",EDGE,{"derivedFrom":sQuery(id+"F4.wireOp",EDGE,"E86.0")}),1.0]])]});
            var sketch = newSketch(context, id + "F8", { "sketchPlane" : qUnion([Q0])});
            skLineSegment(sketch, "E168.bottom", {"start": v(16.75, 0) * mm, "end": v(22.75, 0) * mm});
            skLineSegment(sketch, "E168.top", {"start": v(16.75, -2) * mm, "end": v(22.75, -2) * mm});
            skLineSegment(sketch, "E168.left", {"start": v(16.75, 0) * mm, "end": v(16.75, -2) * mm});
            skLineSegment(sketch, "E168.right", {"start": v(22.75, 0) * mm, "end": v(22.75, -2) * mm});
            skLineSegment(sketch, "E169.MirrorCS", {"start": v(-22.75, 0) * mm, "end": v(-22.75, -2) * mm});
            skLineSegment(sketch, "E170.MirrorCS", {"start": v(-16.75, 0) * mm, "end": v(-16.75, -2) * mm});
            skLineSegment(sketch, "E171.MirrorCS", {"start": v(-16.75, -2) * mm, "end": v(-22.75, -2) * mm});
            skLineSegment(sketch, "E172.MirrorCS", {"start": v(-16.75, 0) * mm, "end": v(-22.75, 0) * mm});
            skSolve(sketch);
        }
        {
            var Q0;
            Q0 = qSketchRegion(id + "F8", true);
            extrude(context, id + "F9", {"entities" : qUnion([Q0]), "operationType" : NewBodyOperationType.ADD, "depth" : 1.5 * mm});
        }
    });
